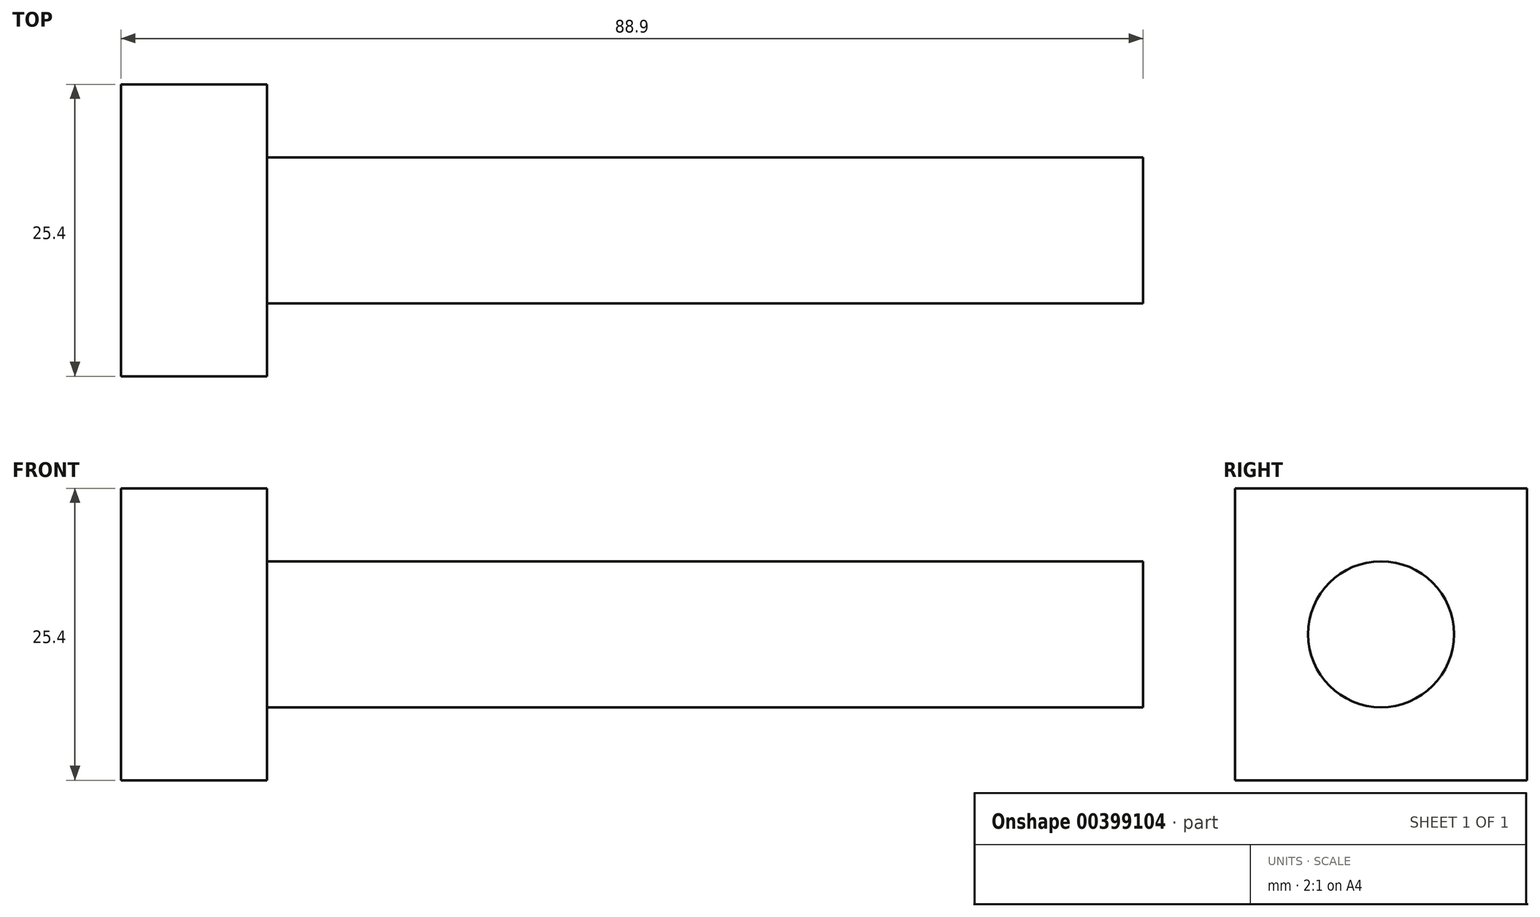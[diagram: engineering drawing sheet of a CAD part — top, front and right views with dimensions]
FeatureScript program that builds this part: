
annotation { "Feature Type Name" : "Feature", "Feature Type Description" : "" }
export const myFeature = defineFeature(function(context is Context, id is Id, definition is map)
    precondition{}
    {
        {
            var Q0;
            Q0=qCreatedBy(makeId("Right.planeOp"),FACE);
            var sketch = newSketch(context, id + "F0", { "sketchPlane" : qUnion([Q0])});
            skLineSegment(sketch, "E0.bottom", {"start": v(-12.7, -12.7) * mm, "end": v(12.7, -12.7) * mm});
            skLineSegment(sketch, "E0.top", {"start": v(-12.7, 12.7) * mm, "end": v(12.7, 12.7) * mm});
            skLineSegment(sketch, "E0.left", {"start": v(-12.7, -12.7) * mm, "end": v(-12.7, 12.7) * mm});
            skLineSegment(sketch, "E0.right", {"start": v(12.7, -12.7) * mm, "end": v(12.7, 12.7) * mm});
            skPoint(sketch, "E0.middle", {"position": v(0, 0) * mm});
            skSolve(sketch);
        }
        {
            var Q0;
            Q0=makeQuery(id+"F0.imprint","IMPRINT",FACE,{"disambiguationData":[TD([[makeQuery(id+"F0.imprint","IMPRINT",EDGE,{"derivedFrom":sQuery(id+"F0.wireOp",EDGE,"E0.bottom")}),1.0]])]});
            extrude(context, id + "F1", {"entities" : qUnion([Q0]), "depth" : 12.7 * mm});
        }
        {
            var Q0;
            Q0=makeQuery(id+"F1.opExtrude","CAP_FACE",FACE,{"disambiguationData":[OSD([sQuery(id+"F0.wireOp",EDGE,"E0.bottom"),sQuery(id+"F0.wireOp",EDGE,"E0.top"),sQuery(id+"F0.wireOp",EDGE,"E0.left"),sQuery(id+"F0.wireOp",EDGE,"E0.right")])],"isStart":false});
            var sketch = newSketch(context, id + "F2", { "sketchPlane" : qUnion([Q0])});
            skCircle(sketch, "E1", {"center": v(0, 0) * mm, "radius": 6.35 * mm});
            skSolve(sketch);
        }
        {
            var Q0;
            Q0=makeQuery(id+"F2.imprint","IMPRINT",FACE,{"disambiguationData":[TD([[makeQuery(id+"F2.imprint","IMPRINT",EDGE,{"derivedFrom":sQuery(id+"F2.wireOp",EDGE,"E1")}),1.0]])]});
            extrude(context, id + "F3", {"entities" : qUnion([Q0]), "operationType" : NewBodyOperationType.ADD, "depth" : 76.2 * mm});
        }
    });
